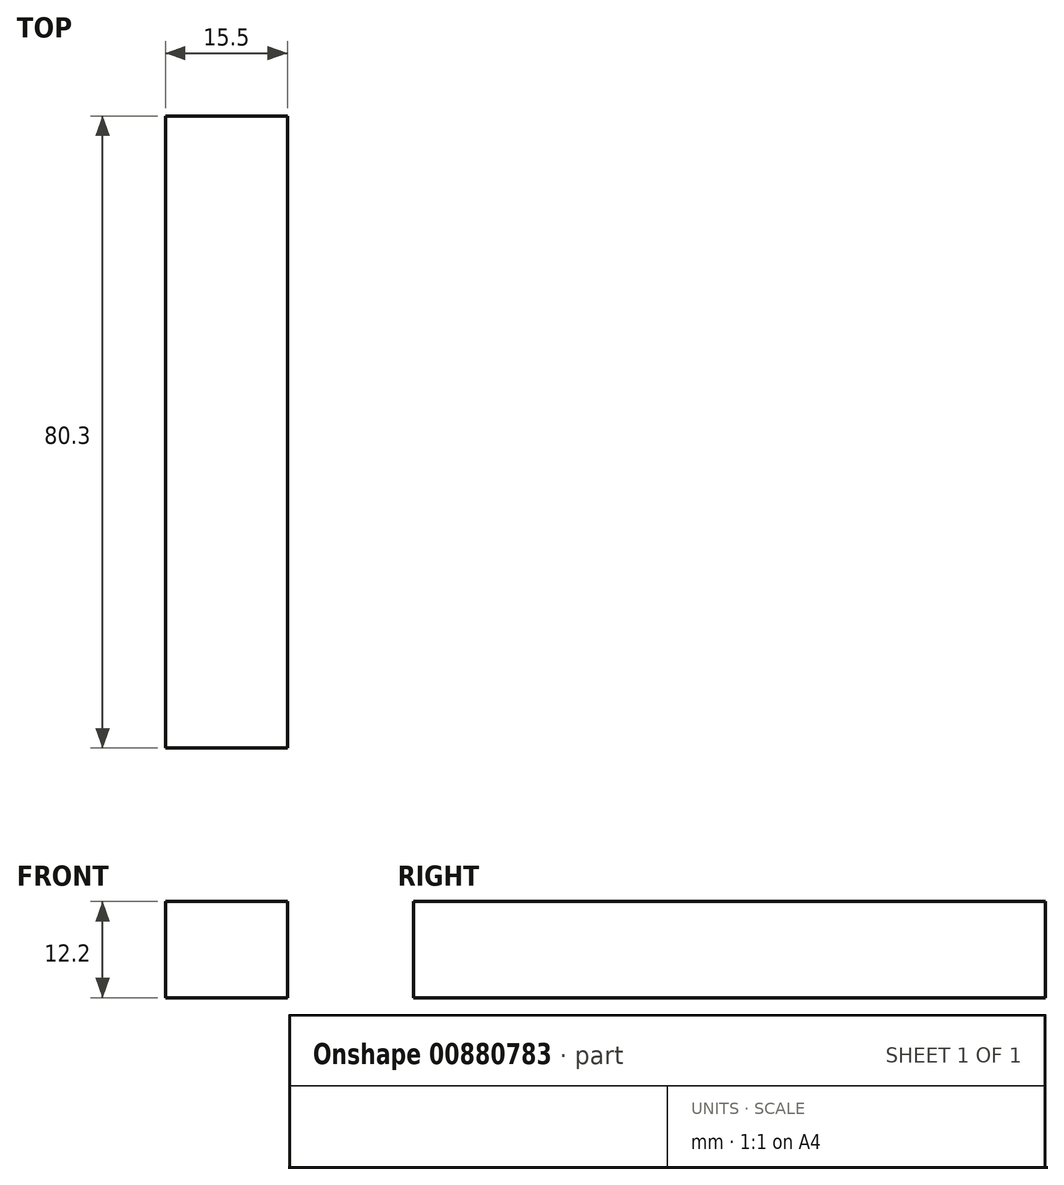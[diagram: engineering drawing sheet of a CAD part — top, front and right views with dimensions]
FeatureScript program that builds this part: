
annotation { "Feature Type Name" : "Feature", "Feature Type Description" : "" }
export const myFeature = defineFeature(function(context is Context, id is Id, definition is map)
    precondition{}
    {
        {
            var Q0;
            Q0=qCreatedBy(makeId("Top.planeOp"),FACE);
            var sketch = newSketch(context, id + "F0", { "sketchPlane" : qUnion([Q0])});
            skLineSegment(sketch, "E0.bottom", {"start": v(-55.08, 9.21) * mm, "end": v(-39.58, 9.21) * mm});
            skLineSegment(sketch, "E0.top", {"start": v(-55.08, -71.1) * mm, "end": v(-39.58, -71.1) * mm});
            skLineSegment(sketch, "E0.left", {"start": v(-55.08, 9.21) * mm, "end": v(-55.08, -71.1) * mm});
            skLineSegment(sketch, "E0.right", {"start": v(-39.58, 9.21) * mm, "end": v(-39.58, -71.1) * mm});
            skSolve(sketch);
        }
        {
            var Q0;
            Q0=makeQuery(id+"F0.imprint","IMPRINT",FACE,{"disambiguationData":[TD([[makeQuery(id+"F0.imprint","IMPRINT",EDGE,{"derivedFrom":sQuery(id+"F0.wireOp",EDGE,"E0.bottom")}),-1.0]])]});
            extrude(context, id + "F1", {"entities" : qUnion([Q0]), "depth" : 12.2 * mm, "offsetDistance" : 25 * mm});
        }
    });
